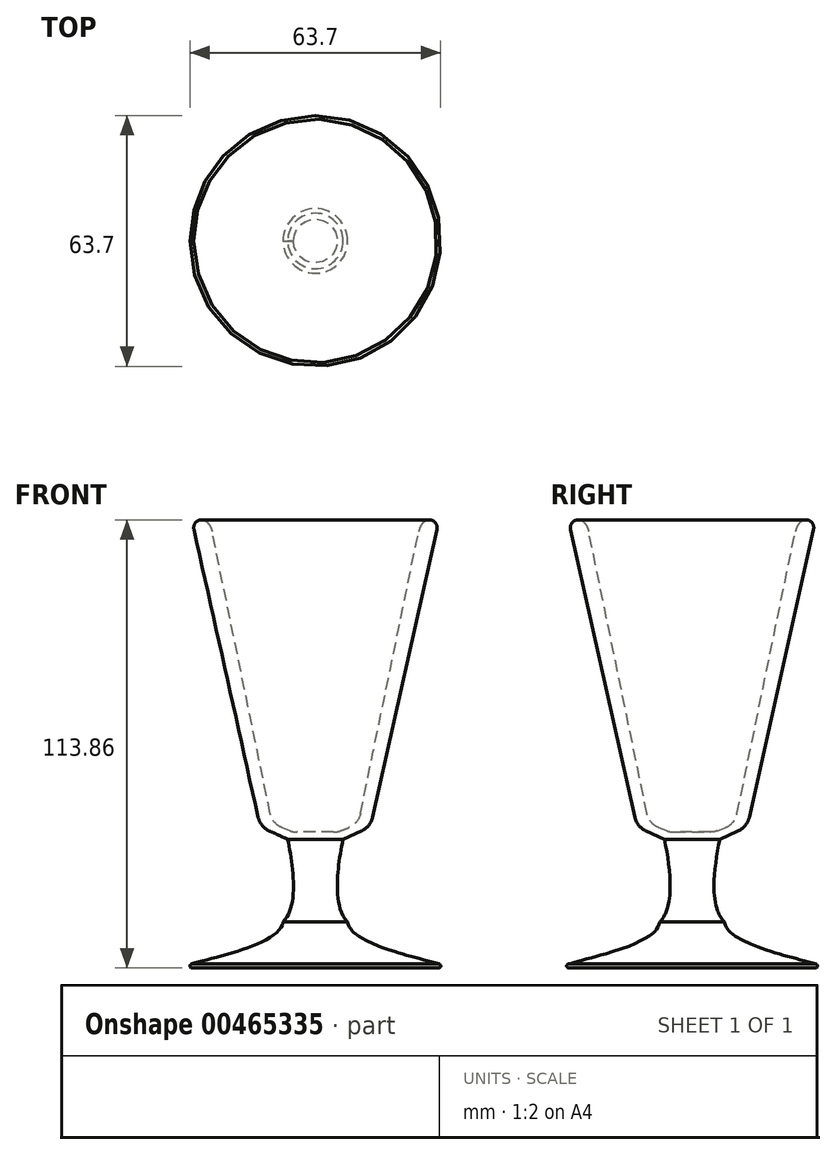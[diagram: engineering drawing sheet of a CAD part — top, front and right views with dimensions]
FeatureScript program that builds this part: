
annotation { "Feature Type Name" : "Feature", "Feature Type Description" : "" }
export const myFeature = defineFeature(function(context is Context, id is Id, definition is map)
    precondition{}
    {
        {
            var Q0;
            Q0=qCreatedBy(makeId("Front.planeOp"),FACE);
            var sketch = newSketch(context, id + "F0", { "sketchPlane" : qUnion([Q0])});
            skLineSegment(sketch, "E0", {"start": v(0, 0) * mm, "end": v(-33.62, 0) * mm});
            skFitSpline(sketch, "E1", {"points": [v(-33.62, 0) * mm, v(-8.2, 11.73) * mm], "startDerivative": vector(2.03, 4.94) * mm, "endDerivative": vector(2.35, 20.72) * mm});
            skFitSpline(sketch, "E2", {"points": [v(-8.2, 11.73) * mm, v(-7.04, 32.7) * mm], "startDerivative": vector(12.5, 12.12) * mm, "endDerivative": vector(-3.9, 19.16) * mm});
            skLineSegment(sketch, "E3", {"start": v(-7.04, 32.7) * mm, "end": v(-13.99, 35.85) * mm});
            skLineSegment(sketch, "E4", {"start": v(-13.99, 35.85) * mm, "end": v(-31.63, 114.86) * mm});
            skLineSegment(sketch, "E5", {"start": v(-31.63, 114.86) * mm, "end": v(-27.07, 114.86) * mm});
            skLineSegment(sketch, "E6", {"start": v(-27.07, 114.86) * mm, "end": v(-10.91, 36.6) * mm});
            skLineSegment(sketch, "E7", {"start": v(-10.91, 36.6) * mm, "end": v(-5.57, 34.5) * mm});
            skLineSegment(sketch, "E8", {"start": v(-5.57, 34.5) * mm, "end": v(0, 34.5) * mm});
            skLineSegment(sketch, "E9", {"start": v(0, 34.5) * mm, "end": v(0, 0) * mm});
            skSolve(sketch);
        }
        {
            var Q0;
            Q0=qCreatedBy(makeId("Front.planeOp"),FACE);
            var sketch = newSketch(context, id + "F1", { "sketchPlane" : qUnion([Q0])});
            skLineSegment(sketch, "E10", {"start": v(0, -17.36) * mm, "end": v(0, 117.9) * mm, "construction": true});
            skSolve(sketch);
        }
        {
            var Q0;
            Q0 = qSketchRegion(id + "F0", true);
            var Q1;
            Q1=sQuery(id+"F1.wireOp",EDGE,"E10");
            revolve(context, id + "F2", {"entities" : qUnion([Q0]), "axis" : qUnion([Q1]), "revolveType" : RevolveType.FULL});
        }
        {
            var Q0;
            Q0=makeQuery(id+"F2.opRevolve","SWEPT_EDGE",EDGE,{"disambiguationData":[OSD([sQuery(id+"F0.wireOp",EDGE,"E0"),sQuery(id+"F0.wireOp",EDGE,"E1")])]});
            fillet(context, id + "F3", {"entities" : qUnion([Q0]), "radius" : 0.5 * mm, "tangentPropagation" : true, "allowEdgeOverflow" : false});
        }
        {
            var Q0;
            Q0=makeQuery(id+"F2.opRevolve","SWEPT_EDGE",EDGE,{"disambiguationData":[OSD([sQuery(id+"F0.wireOp",EDGE,"E3"),sQuery(id+"F0.wireOp",EDGE,"E4")])]});
            fillet(context, id + "F4", {"entities" : qUnion([Q0]), "radius" : 5 * mm, "tangentPropagation" : true, "allowEdgeOverflow" : false});
        }
        {
            var Q0;
            Q0=makeQuery(id+"F2.opRevolve","SWEPT_EDGE",EDGE,{"disambiguationData":[OSD([sQuery(id+"F0.wireOp",EDGE,"E5"),sQuery(id+"F0.wireOp",EDGE,"E6")])]});
            fillet(context, id + "F5", {"entities" : qUnion([Q0]), "radius" : 5 * mm, "tangentPropagation" : true, "allowEdgeOverflow" : false});
        }
        {
            var Q0;
            Q0=makeQuery(id+"F2.opRevolve","SWEPT_EDGE",EDGE,{"disambiguationData":[OSD([sQuery(id+"F0.wireOp",EDGE,"E4"),sQuery(id+"F0.wireOp",EDGE,"E5")])]});
            fillet(context, id + "F6", {"entities" : qUnion([Q0]), "radius" : 2 * mm, "tangentPropagation" : true, "allowEdgeOverflow" : false});
        }
        {
            var Q0;
            Q0=makeQuery(id+"F2.opRevolve","SWEPT_EDGE",EDGE,{"disambiguationData":[OSD([sQuery(id+"F0.wireOp",EDGE,"E6"),sQuery(id+"F0.wireOp",EDGE,"E7")])]});
            fillet(context, id + "F7", {"entities" : qUnion([Q0]), "radius" : 5 * mm, "tangentPropagation" : true, "allowEdgeOverflow" : false});
        }
        {
            var Q0;
            Q0=makeQuery(id+"F2.opRevolve","SWEPT_EDGE",EDGE,{"disambiguationData":[OSD([sQuery(id+"F0.wireOp",EDGE,"E7"),sQuery(id+"F0.wireOp",EDGE,"E8")])]});
            fillet(context, id + "F8", {"entities" : qUnion([Q0]), "radius" : 5 * mm, "tangentPropagation" : true, "allowEdgeOverflow" : false});
        }
    });
